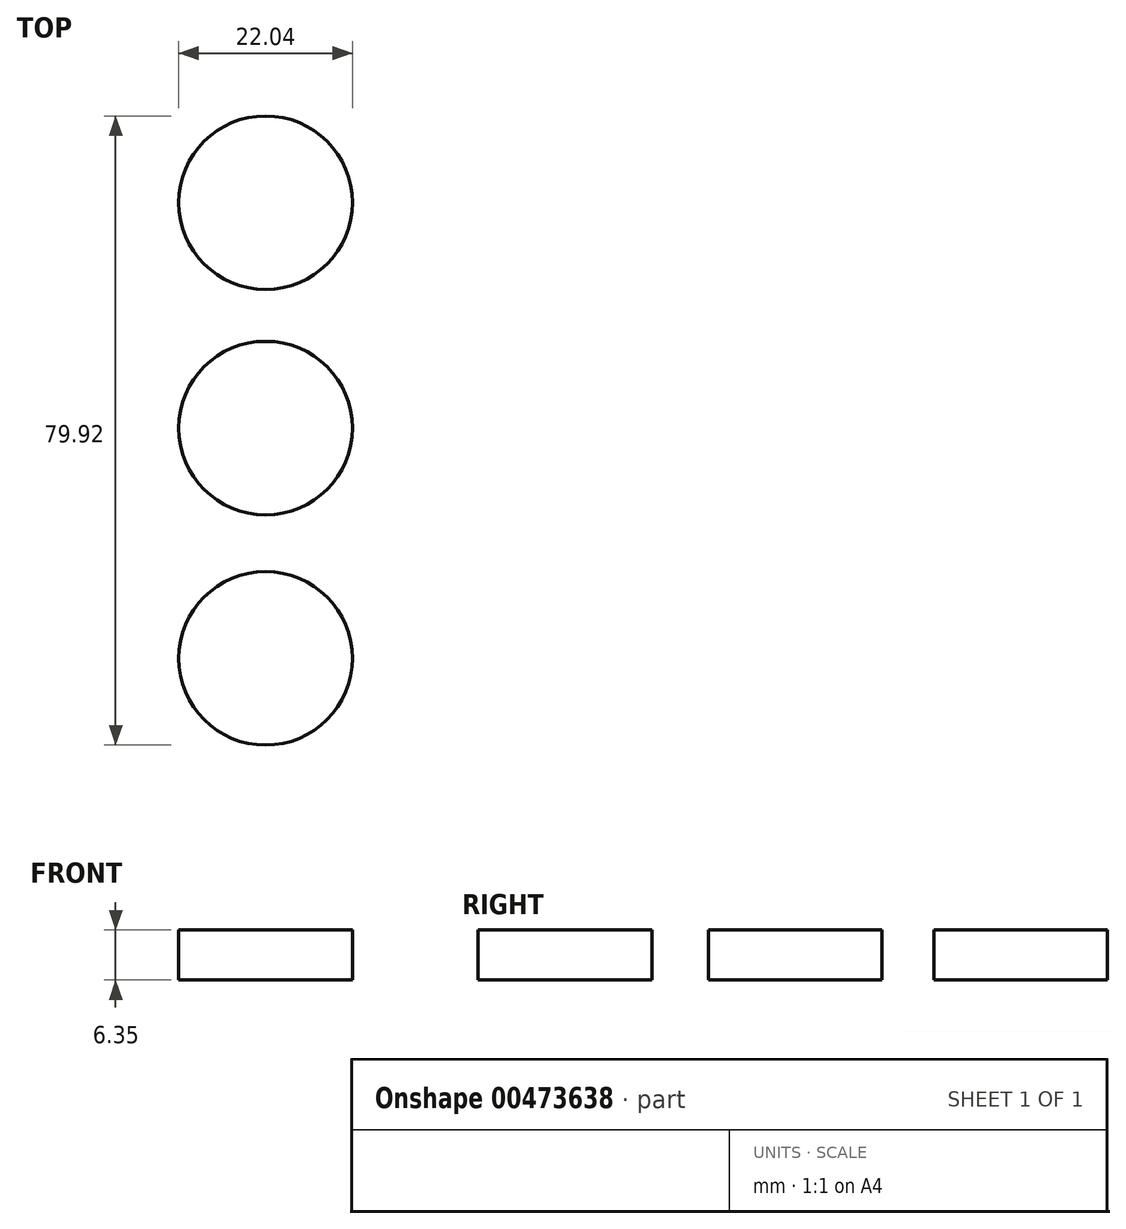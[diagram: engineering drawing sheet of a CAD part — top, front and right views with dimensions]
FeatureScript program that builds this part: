
annotation { "Feature Type Name" : "Feature", "Feature Type Description" : "" }
export const myFeature = defineFeature(function(context is Context, id is Id, definition is map)
    precondition{}
    {
        {
            var Q0;
            Q0=qCreatedBy(makeId("Top.planeOp"),FACE);
            var sketch = newSketch(context, id + "F0", { "sketchPlane" : qUnion([Q0])});
            skCircle(sketch, "E0", {"center": v(0, 0) * mm, "radius": 11.02 * mm});
            skSolve(sketch);
        }
        {
            var Q0;
            Q0=qCreatedBy(makeId("Top.planeOp"),FACE);
            var sketch = newSketch(context, id + "F1", { "sketchPlane" : qUnion([Q0])});
            skCircle(sketch, "E1", {"center": v(0, 28.63) * mm, "radius": 11.02 * mm});
            skCircle(sketch, "E2", {"center": v(0, -29.25) * mm, "radius": 11.02 * mm});
            skLineSegment(sketch, "E3", {"start": v(4.3, 18.48) * mm, "end": v(4.3, 10.37) * mm});
            skLineSegment(sketch, "E4", {"start": v(-5.05, 18.83) * mm, "end": v(-5.05, 10.7) * mm});
            skLineSegment(sketch, "E5", {"start": v(4.3, -10.97) * mm, "end": v(4.3, -19.1) * mm});
            skLineSegment(sketch, "E6", {"start": v(-5.05, -10.68) * mm, "end": v(-5.05, -19.45) * mm});
            skSolve(sketch);
        }
        {
            var Q0;
            Q0 = qSketchRegion(id + "F0", true);
            var Q1;
            Q1 = qSketchRegion(id + "F1", true);
            extrude(context, id + "F2", {"entities" : qUnion([Q0, Q1]), "depth" : 6.35 * mm});
        }
    });
